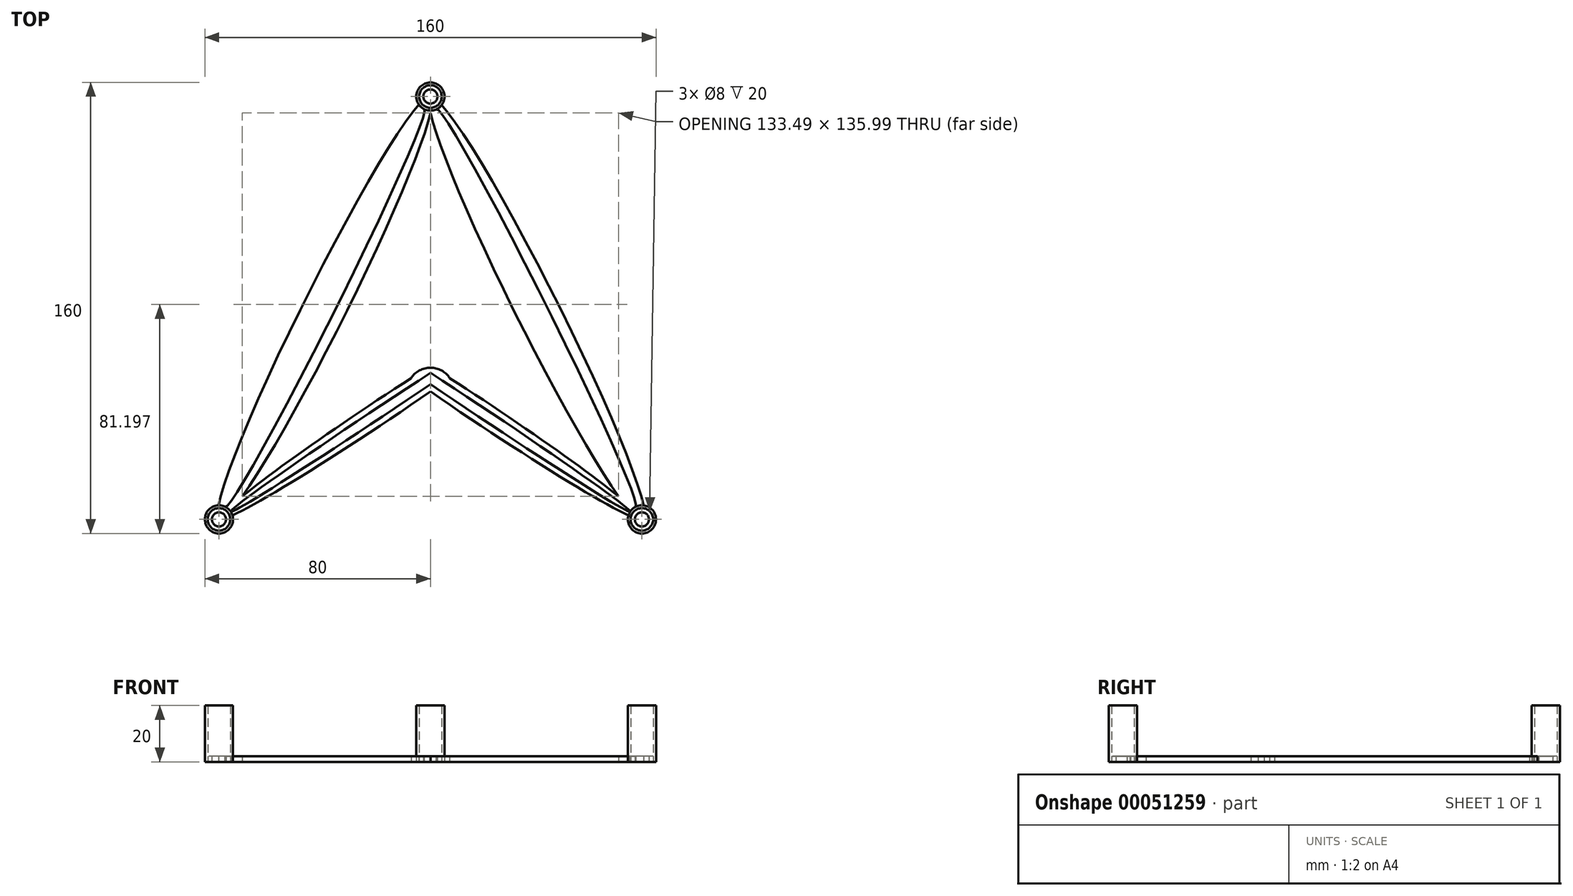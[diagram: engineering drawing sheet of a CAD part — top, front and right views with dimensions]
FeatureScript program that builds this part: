
annotation { "Feature Type Name" : "Feature", "Feature Type Description" : "" }
export const myFeature = defineFeature(function(context is Context, id is Id, definition is map)
    precondition{}
    {
        {
            var Q0;
            Q0=qCreatedBy(makeId("Top.planeOp"),FACE);
            var sketch = newSketch(context, id + "F0", { "sketchPlane" : qUnion([Q0])});
            skCircle(sketch, "E0", {"center": v(0, 0) * mm, "radius": 5 * mm});
            skCircle(sketch, "E1", {"center": v(0, 0) * mm, "radius": 4 * mm});
            skCircle(sketch, "E2", {"center": v(150, 0) * mm, "radius": 5 * mm});
            skCircle(sketch, "E3", {"center": v(150, 0) * mm, "radius": 4 * mm});
            skCircle(sketch, "E4", {"center": v(75, 150) * mm, "radius": 5 * mm});
            skCircle(sketch, "E5", {"center": v(75, 150) * mm, "radius": 4 * mm});
            skLineSegment(sketch, "E6", {"start": v(75, 150) * mm, "end": v(0, 0) * mm, "construction": true});
            skLineSegment(sketch, "E7", {"start": v(150, 0) * mm, "end": v(77.24, 145.53) * mm, "construction": true});
            skPoint(sketch, "E8", {"position": v(37.5, 75) * mm});
            skPoint(sketch, "E9", {"position": v(112.5, 75) * mm});
            skLineSegment(sketch, "E10", {"start": v(0, 0) * mm, "end": v(147, 0) * mm, "construction": true});
            skLineSegment(sketch, "E11", {"start": v(75, 150) * mm, "end": v(75, 0) * mm, "construction": true});
            skPoint(sketch, "E12", {"position": v(75, 75) * mm});
            skPoint(sketch, "E13", {"position": v(75, 0) * mm});
            skEllipticalArc(sketch, "E14.MirrorC", {});
            skLineSegment(sketch, "E15", {"start": v(112.5, 75) * mm, "end": v(0, 0) * mm, "construction": true});
            skLineSegment(sketch, "E16", {"start": v(37.5, 75) * mm, "end": v(150, 0) * mm, "construction": true});
            skEllipticalArc(sketch, "E17.trimOffspring", {});
            skPoint(sketch, "E18", {"position": v(56.25, 37.5) * mm});
            skPoint(sketch, "E19", {"position": v(93.75, 37.5) * mm});
            skEllipticalArc(sketch, "E20.MirrorC", {});
            skEllipticalArc(sketch, "E21.trimOffspring", {});
            skEllipticalArc(sketch, "E22.trimOffspring", {});
            skPoint(sketch, "E23", {"position": v(81.83, 50.15) * mm});
            skPoint(sketch, "E24", {"position": v(75, 45.36) * mm});
            skEllipticalArc(sketch, "E25.trimOffspring", {});
            skEllipticalArc(sketch, "E26.trimOffspring", {});
            skEllipticalArc(sketch, "E27.trimOffspring", {});
            skEllipticalArc(sketch, "E28.trimOffspring", {});
            skEllipticalArc(sketch, "E29.trimOffspring", {});
            skEllipticalArc(sketch, "E30.trimOffspring", {});
            skLineSegment(sketch, "E31.trimOffspring", {"start": v(76.79, 146.42) * mm, "end": v(75, 150) * mm, "construction": true});
            skEllipticalArc(sketch, "E32.trimOffspring", {});
            skEllipticalArc(sketch, "E33.trimOffspring", {});
            skPoint(sketch, "E34", {"position": v(2.24, 4.47) * mm});
            skPoint(sketch, "E35", {"position": v(4.16, 2.77) * mm});
            skPoint(sketch, "E36", {"position": v(147.76, 4.47) * mm});
            skPoint(sketch, "E37", {"position": v(145.84, 2.77) * mm});
            skEllipse(sketch, "E38", {"center": v(37.5, 75) * mm, "majorRadius": 78.85 * mm, "minorRadius": 3.6 * mm, "majorAxis": v(-0.45, -0.9)});
            skEllipse(sketch, "E39.MirrorC", {"center": v(112.5, 75) * mm, "majorRadius": 78.85 * mm, "minorRadius": 3.6 * mm, "majorAxis": v(0.45, -0.9)});
            skEllipticalArc(sketch, "E40", {});
            skEllipticalArc(sketch, "E41.trimOffspring", {});
            skArc(sketch, "E42", {"start": v(81.83, 50.15) * mm, "mid": v(75, 53.81) * mm, "end": v(68.17, 50.15) * mm});
            skLineSegment(sketch, "E43", {"start": v(0, -5) * mm, "end": v(150, -5) * mm, "construction": true});
            skCircle(sketch, "E44", {"center": v(0, 0) * mm, "radius": 2.5 * mm});
            skCircle(sketch, "E45", {"center": v(150, 0) * mm, "radius": 2.5 * mm});
            skCircle(sketch, "E46", {"center": v(75, 150) * mm, "radius": 2.5 * mm});
            const initialGuessF0  = {"E14.MirrorC": [0.11272642147523293, 0.07462351626781064, -0.4491181731093815, 0.8934723647561192, 0.08409790807462164, 0.007533898815560416, 3.483486498382255, 5.9626459504802], "E17.trimOffspring": [0.0375, 0.075, 0.4472135955034311, 0.8944271909981794, 0.08385254915624216, 0.007495930562586505, 3.66025564937617, 4.678609657111362], "E20.MirrorC": [0.09375, 0.0375, -0.8320502943378456, 0.5547001962252263, 0.06760408641494979, 0.004037122288040243, 6.2831853071795845, 0.014929006220298862], "E21.trimOffspring": [0.05625, 0.0375, 0.8320502943378438, 0.5547001962252289, 0.06760408641494979, 0.004037122288040243, 6.268256300957579, 0], "E22.trimOffspring": [0.05625, 0.0375, 0.8320502943389216, 0.5547001962236122, 0.06760408641494979, 0.004037122288040243, 1.3176094199070696, 2.5518711663737945], "E25.trimOffspring": [0.09375, 0.0375, -0.8320502943378456, 0.5547001962252263, 0.06760408641494979, 0.004037122288040243, 1.2710296626233417, 2.763580836347638], "E26.trimOffspring": [0.09375, 0.0375, -0.8320502943378456, 0.5547001962252263, 0.06760408641494979, 0.004037122288040243, 3.7313141408077475, 4.965575887272516], "E27.trimOffspring": [0.09375, 0.0375, -0.8320502943378456, 0.5547001962252263, 0.06760408641494979, 0.004037122288040243, 3.091838641469476, 3.141592653589794], "E28.trimOffspring": [0.05625, 0.0375, 0.8320502943389216, 0.5547001962236122, 0.06760408641494979, 0.004037122288040243, 3.5196044708348504, 5.012155644559556], "E29.trimOffspring": [0.0375, 0.075, 0.4472135955034311, 0.8944271909981794, 0.08385254915624216, 0.007495930562586505, 0.325008602608149, 2.8165840510217244], "E30.trimOffspring": [0.1125, 0.075, -0.4472135954999611, 0.8944271909999144, 0.08385254915624216, 0.007495930562586505, 0.35383818370379805, 1.6045756500603638], "E32.trimOffspring": [0.1125, 0.075, -0.4472135954999611, 0.8944271909999144, 0.08385254915624216, 0.007495930562586505, 1.6045756500603638, 2.622929657774568], "E33.trimOffspring": [0.0375, 0.075, 0.4472135955034311, 0.8944271909981794, 0.08385254915624216, 0.007495930562586505, 4.678609657111362, 5.929347123452072], "E40": [0.05625, 0.0375, -0.8320502943399973, -0.5547001962219988, 0.06260408641494977, 0.0017743028876845458, 4.325345275038231, 1.9200556660245232], "E41.trimOffspring": [0.09375, 0.0375, 0.8320502943367691, -0.5547001962268411, 0.06260408641494977, 0.0017743028876845458, 4.363129641155087, 1.9578400321413274]};
            skSetInitialGuess(sketch, initialGuessF0);
            skSolve(sketch);
        }
        {
            var Q0;
            Q0=makeQuery(id+"F0.imprint","IMPRINT",FACE,{"disambiguationData":[TD([[makeQuery(id+"F0.imprint","IMPRINT",EDGE,{"derivedFrom":sQuery(id+"F0.wireOp",EDGE,"E1")}),1.0]])]});
            var Q1;
            Q1=makeQuery(id+"F0.imprint","IMPRINT",FACE,{"disambiguationData":[TD([[makeQuery(id+"F0.imprint","IMPRINT",EDGE,{"derivedFrom":sQuery(id+"F0.wireOp",EDGE,"E3")}),1.0]])]});
            var Q2;
            Q2=makeQuery(id+"F0.imprint","IMPRINT",FACE,{"disambiguationData":[TD([[makeQuery(id+"F0.imprint","IMPRINT",EDGE,{"derivedFrom":sQuery(id+"F0.wireOp",EDGE,"E5")}),1.0]])]});
            var Q3;
            {var subQ0=sQuery(id+"F0.wireOp",EDGE,"E14.MirrorC");Q3=makeQuery(id+"F0.imprint","IMPRINT",FACE,{"disambiguationData":[TD([[makeQuery(id+"F0.imprint","IMPRINT",EDGE,{"derivedFrom":subQ0}),1.0]])]});}
            var Q4;
            {var subQ1=sQuery(id+"F0.wireOp",EDGE,"E17.trimOffspring");Q4=makeQuery(id+"F0.imprint","IMPRINT",FACE,{"disambiguationData":[TD([[makeQuery(id+"F0.imprint","IMPRINT",EDGE,{"derivedFrom":subQ1}),1.0]])]});}
            var Q5;
            {var subQ4=sQuery(id+"F0.wireOp",EDGE,"E25.trimOffspring");Q5=makeQuery(id+"F0.imprint","IMPRINT",FACE,{"disambiguationData":[TD([[makeQuery(id+"F0.imprint","IMPRINT",EDGE,{"derivedFrom":subQ4}),1.0]])]});}
            var Q6;
            {var subQ0=sQuery(id+"F0.wireOp",EDGE,"E29.trimOffspring");Q6=makeQuery(id+"F0.imprint","IMPRINT",FACE,{"disambiguationData":[TD([[makeQuery(id+"F0.imprint","IMPRINT",EDGE,{"derivedFrom":subQ0}),1.0]])]});}
            extrude(context, id + "F1", {"entities" : qUnion([Q0, Q1, Q2, Q3, Q4, Q5, Q6]), "depth" : 2 * mm});
        }
        {
            var Q0;
            Q0=makeQuery(id+"F0.imprint","IMPRINT",FACE,{"disambiguationData":[TD([[makeQuery(id+"F0.imprint","IMPRINT",EDGE,{"derivedFrom":sQuery(id+"F0.wireOp",EDGE,"E1")}),-1.0]])]});
            var Q1;
            Q1=makeQuery(id+"F0.imprint","IMPRINT",FACE,{"disambiguationData":[TD([[makeQuery(id+"F0.imprint","IMPRINT",EDGE,{"derivedFrom":sQuery(id+"F0.wireOp",EDGE,"E3")}),-1.0]])]});
            var Q2;
            Q2=makeQuery(id+"F0.imprint","IMPRINT",FACE,{"disambiguationData":[TD([[makeQuery(id+"F0.imprint","IMPRINT",EDGE,{"derivedFrom":sQuery(id+"F0.wireOp",EDGE,"E5")}),-1.0]])]});
            extrude(context, id + "F2", {"entities" : qUnion([Q0, Q1, Q2]), "depth" : 20 * mm});
        }
    });
